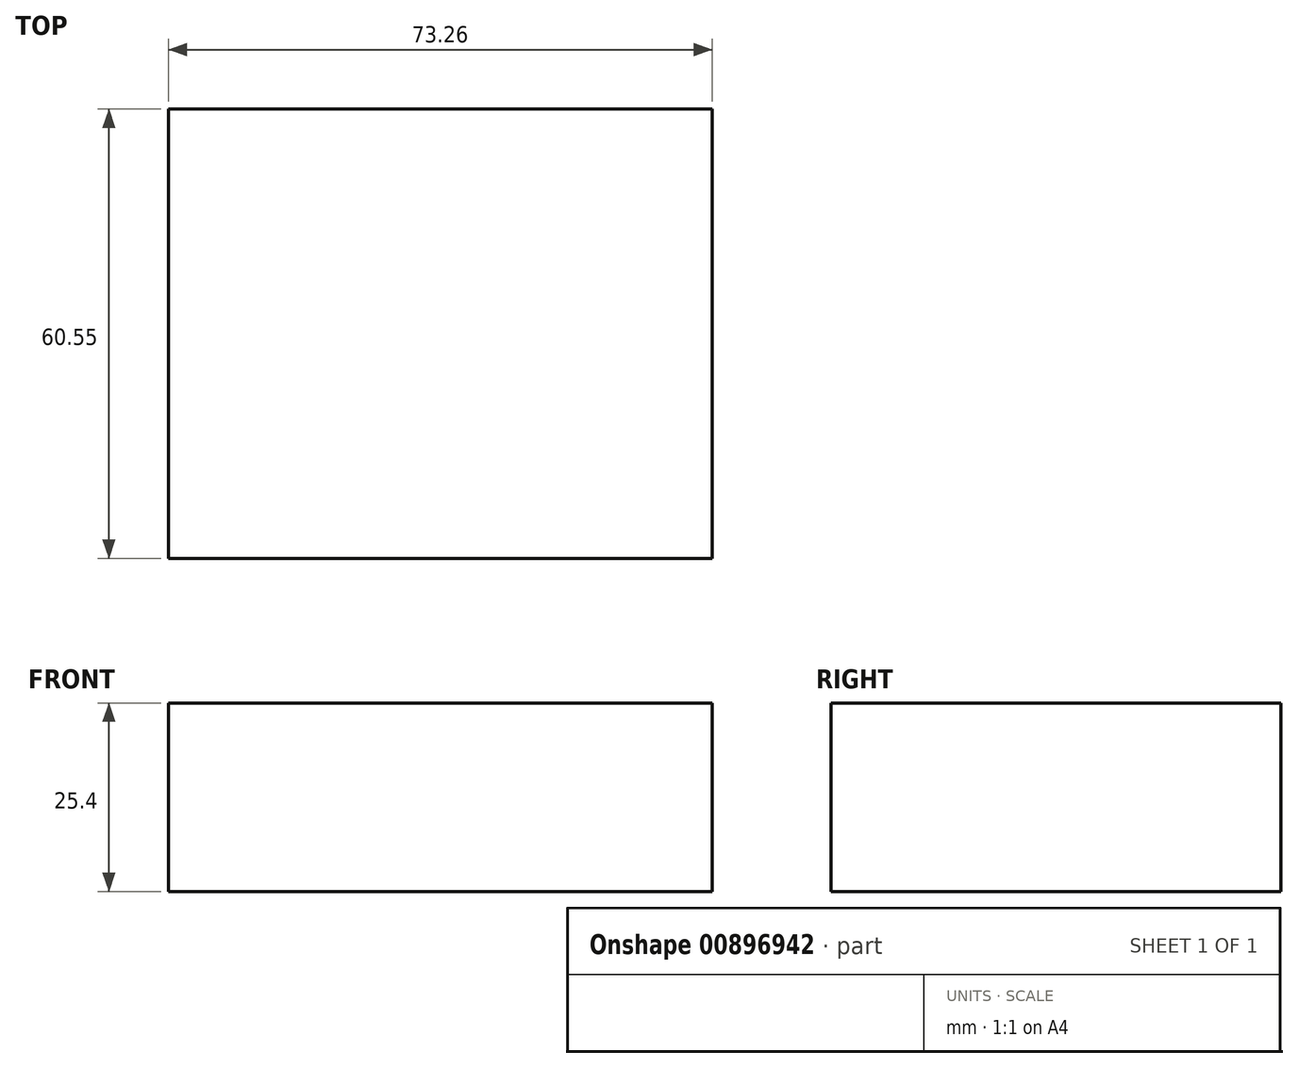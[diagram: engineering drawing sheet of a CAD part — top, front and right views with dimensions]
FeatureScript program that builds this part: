
annotation { "Feature Type Name" : "Feature", "Feature Type Description" : "" }
export const myFeature = defineFeature(function(context is Context, id is Id, definition is map)
    precondition{}
    {
        {
            var Q0;
            Q0=qCreatedBy(makeId("Top.planeOp"),FACE);
            var sketch = newSketch(context, id + "F0", { "sketchPlane" : qUnion([Q0])});
            skLineSegment(sketch, "E0.bottom", {"start": v(-37.52, 31.3) * mm, "end": v(35.74, 31.3) * mm});
            skLineSegment(sketch, "E0.top", {"start": v(-37.52, -29.26) * mm, "end": v(35.74, -29.26) * mm});
            skLineSegment(sketch, "E0.left", {"start": v(-37.52, 31.3) * mm, "end": v(-37.52, -29.26) * mm});
            skLineSegment(sketch, "E0.right", {"start": v(35.74, 31.3) * mm, "end": v(35.74, -29.26) * mm});
            skSolve(sketch);
        }
        {
            var Q0;
            Q0=makeQuery(id+"F0.imprint","IMPRINT",FACE,{"disambiguationData":[TD([[makeQuery(id+"F0.imprint","IMPRINT",EDGE,{"derivedFrom":sQuery(id+"F0.wireOp",EDGE,"E0.bottom")}),-1.0]])]});
            extrude(context, id + "F1", {"entities" : qUnion([Q0]), "depth" : 25.4 * mm, "offsetDistance" : 25.4 * mm});
        }
    });
